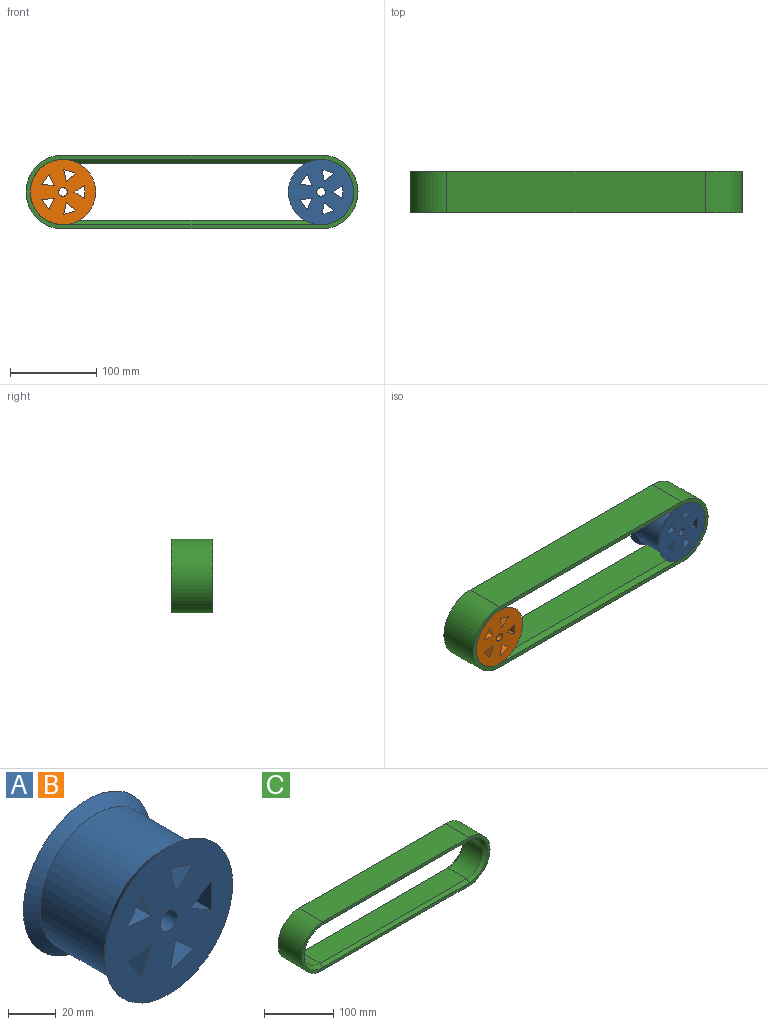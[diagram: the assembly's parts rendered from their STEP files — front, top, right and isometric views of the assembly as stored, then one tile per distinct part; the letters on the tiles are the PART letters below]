
ASSEMBLY  parts=3 mates=2
PART A: 21 faces, bbox 75.9x48.4x75.9 mm
  f0: plane 75.9x75.9mm, normal (0,1,0), area 3984mm2, adj f4,f5,f6,f7,f8,f9,f10,f11
  f1: plane 75.9x75.9mm, normal (0,-1,0), area 3984mm2, adj f2,f5,f6,f7,f8,f9,f10,f11
  f2: cone r=33mm half-angle=45deg, axis (0,-1,0), area 1560.3mm2, adj f1,f3
  f3: cylinder r=33mm len=66mm, axis (0,1,0), area 7982.8mm2, adj f2,f4
  f4: cone r=37.95mm half-angle=45deg, axis (0,1,0), area 1560.3mm2, adj f0,f3
  f5: cylinder r=5mm len=48.4mm, axis (0,1,0), area 1520.5mm2, adj f0,f1
  f6: plane 48.4x12.65mm, normal (0.5,0,0.87), area 707mm2, adj f0,f1,f7,f8
  f7: plane 48.4x12.65mm, normal (0.5,0,-0.87), area 707mm2, adj f0,f1,f6,f8
  f8: plane 48.4x14.61mm, normal (-1,0,0), area 707mm2, adj f0,f1,f6,f7
  f9: plane 48.4x10.86mm, normal (-0.67,0,0.74), area 707mm2, adj f0,f1,f10,f11
  f10: plane 48.4x14.29mm, normal (0.98,0,0.21), area 707mm2, adj f0,f1,f9,f11
  f11: plane 48.4x13.89mm, normal (-0.31,0,-0.95), area 707mm2, adj f0,f1,f9,f10
  f12: plane 48.4x13.34mm, normal (-0.91,0,-0.41), area 707mm2, adj f0,f1,f13,f14
  f13: plane 48.4x14.53mm, normal (0.1,0,0.99), area 707mm2, adj f0,f1,f12,f14
  f14: plane 48.4x11.82mm, normal (0.81,0,-0.59), area 707mm2, adj f0,f1,f12,f13
  f15: plane 48.4x14.53mm, normal (0.1,0,-0.99), area 707mm2, adj f0,f1,f16,f17
  f16: plane 48.4x13.34mm, normal (-0.91,0,0.41), area 707mm2, adj f0,f1,f15,f17
  f17: plane 48.4x11.82mm, normal (0.81,0,0.59), area 707mm2, adj f0,f1,f15,f16
  f18: plane 48.4x14.29mm, normal (0.98,0,-0.21), area 707mm2, adj f0,f1,f19,f20
  f19: plane 48.4x10.86mm, normal (-0.67,0,-0.74), area 707mm2, adj f0,f1,f18,f20
  f20: plane 48.4x13.89mm, normal (-0.31,0,0.95), area 707mm2, adj f0,f1,f18,f19
PART B: same geometry as A
PART C: 18 faces, bbox 385.9x48.4x85.9 mm
  f0: plane 300x48.4mm, normal (0,0,1), area 14519.8mm2, adj f3,f11,f12,f13
  f1: plane 300x4.95mm, normal (0,0.71,-0.71), area 2100mm2, adj f2,f4,f13,f14
  f2: plane 300x38.5mm, normal (0,0,-1), area 11550mm2, adj f1,f5,f15,f17
  f3: cylinder r=42.95mm len=85.9mm, axis (0,1,0), area 6530.6mm2, adj f0,f7,f11,f13
  f4: cone r=33mm half-angle=45deg, axis (0,1,0), area 780.1mm2, adj f1,f5,f8,f13
  f5: cylinder r=33mm len=66mm, axis (0,1,0), area 3991.4mm2, adj f2,f4,f6,f9
  f6: cone r=37.95mm half-angle=45deg, axis (0,-1,0), area 780.1mm2, adj f5,f10,f11,f17
  f7: plane 300x48.4mm, normal (0,0,-1), area 14519.8mm2, adj f3,f11,f12,f13
  f8: plane 300x4.95mm, normal (0,0.71,0.71), area 2100mm2, adj f4,f9,f13,f14
  f9: plane 300x38.5mm, normal (0,0,1), area 11550mm2, adj f5,f8,f10,f15
  f10: plane 300x4.95mm, normal (0,-0.71,0.71), area 2100mm2, adj f6,f9,f11,f16
  f11: plane 385.9x85.9mm, normal (0,-1,0), area 4270.8mm2, adj f0,f3,f6,f7,f10,f12,f16,f17
  f12: cylinder r=42.95mm len=85.9mm, axis (0,1,0), area 6530.6mm2, adj f0,f7,f11,f13
  f13: plane 385.9x85.9mm, normal (0,1,0), area 4270.8mm2, adj f0,f1,f3,f4,f7,f8,f12,f14
  f14: cone r=33mm half-angle=45deg, axis (0,1,0), area 780.1mm2, adj f1,f8,f13,f15
  f15: cylinder r=33mm len=66mm, axis (0,1,0), area 3991.4mm2, adj f2,f9,f14,f16
  f16: cone r=37.95mm half-angle=45deg, axis (0,-1,0), area 780.1mm2, adj f10,f11,f15,f17
  f17: plane 300x4.95mm, normal (0,-0.71,-0.71), area 2100mm2, adj f2,f6,f11,f16
PLACE A at identity
PLACE B t=(-300,0,0)mm
PLACE C at identity fixed
MATE revolute A.f2 <-> C.f12  axis (0,1,0) through (0,0,0)mm
MATE revolute B.f2 <-> C.f3  axis (0,1,0) through (-300,0,0)mm
